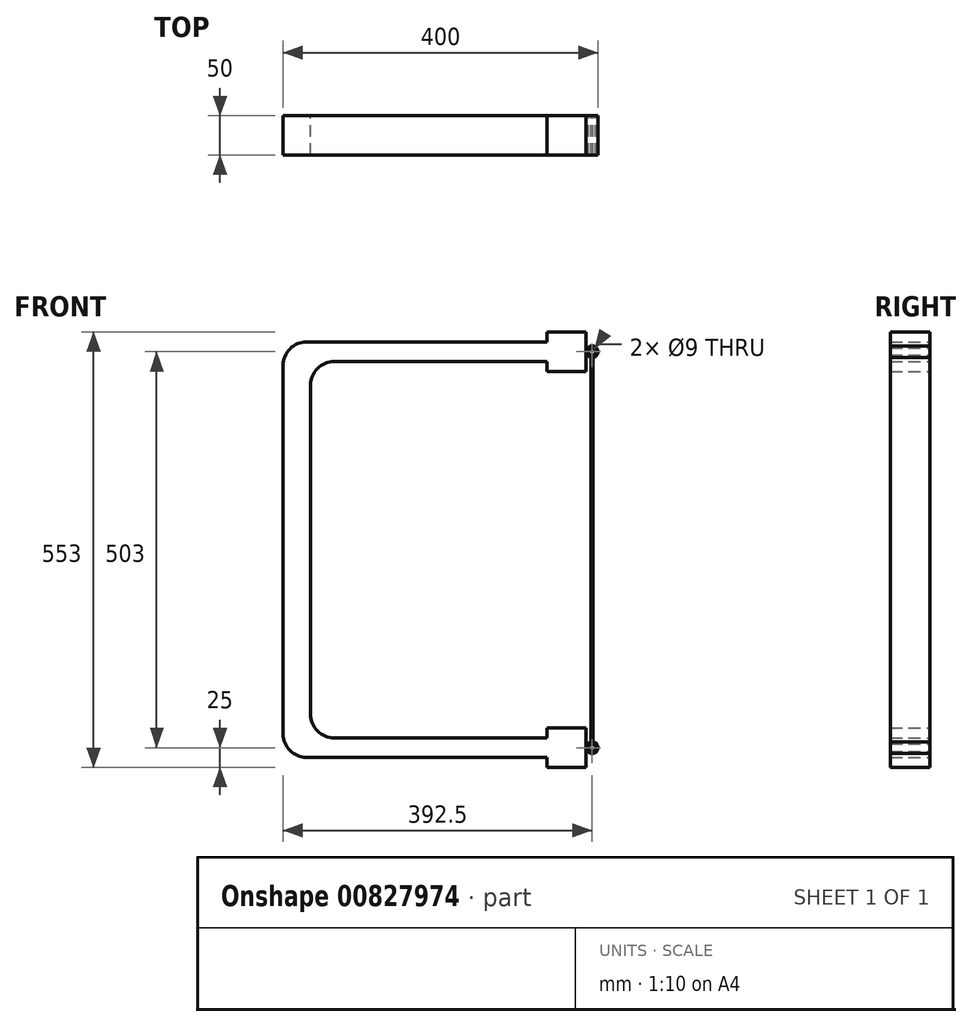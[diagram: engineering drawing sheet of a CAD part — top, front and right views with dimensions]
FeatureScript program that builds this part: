
annotation { "Feature Type Name" : "Feature", "Feature Type Description" : "" }
export const myFeature = defineFeature(function(context is Context, id is Id, definition is map)
    precondition{}
    {
        {
            var Q0;
            Q0=qCreatedBy(makeId("Front.planeOp"),FACE);
            var sketch = newSketch(context, id + "F0", { "sketchPlane" : qUnion([Q0])});
            skLineSegment(sketch, "E0.bottom", {"start": v(135, 264) * mm, "end": v(-170, 264) * mm});
            skLineSegment(sketch, "E0.left", {"start": v(200, 264) * mm, "end": v(200, 239) * mm, "construction": true});
            skLineSegment(sketch, "E0.right", {"start": v(-200, 234) * mm, "end": v(-200, -234) * mm});
            skPoint(sketch, "E0.middle", {"position": v(0, 0) * mm});
            skLineSegment(sketch, "E1.bottom", {"start": v(135, 239) * mm, "end": v(-135, 239) * mm});
            skLineSegment(sketch, "E1.top", {"start": v(135, -239) * mm, "end": v(-135, -239) * mm});
            skLineSegment(sketch, "E1.right", {"start": v(-165, 209) * mm, "end": v(-165, -209) * mm});
            skLineSegment(sketch, "E2.trimOffspring", {"start": v(200, -239) * mm, "end": v(200, -264) * mm, "construction": true});
            skPoint(sketch, "E3.visualSharp", {"position": v(-200, 264) * mm});
            skArc(sketch, "E3.filletArc", {"start": v(-170, 264) * mm, "mid": v(-191.21, 255.21) * mm, "end": v(-200, 234) * mm});
            skPoint(sketch, "E4.visualSharp", {"position": v(-165, 239) * mm});
            skArc(sketch, "E4.filletArc", {"start": v(-135, 239) * mm, "mid": v(-156.21, 230.21) * mm, "end": v(-165, 209) * mm});
            skPoint(sketch, "E5.visualSharp", {"position": v(-200, -264) * mm});
            skArc(sketch, "E5.filletArc", {"start": v(-200, -234) * mm, "mid": v(-191.21, -255.21) * mm, "end": v(-170, -264) * mm});
            skPoint(sketch, "E6.visualSharp", {"position": v(-165, -239) * mm});
            skArc(sketch, "E6.filletArc", {"start": v(-165, -209) * mm, "mid": v(-156.21, -230.21) * mm, "end": v(-135, -239) * mm});
            skLineSegment(sketch, "E7.top", {"start": v(185, 276.5) * mm, "end": v(135, 276.5) * mm});
            skLineSegment(sketch, "E7.right", {"start": v(135, 264) * mm, "end": v(135, 276.5) * mm});
            skLineSegment(sketch, "E8.top", {"start": v(185, 226.5) * mm, "end": v(135, 226.5) * mm});
            skLineSegment(sketch, "E8.right", {"start": v(135, 239) * mm, "end": v(135, 226.5) * mm});
            skLineSegment(sketch, "E9.top", {"start": v(185, -226.5) * mm, "end": v(135, -226.5) * mm});
            skLineSegment(sketch, "E9.right", {"start": v(135, -239) * mm, "end": v(135, -226.5) * mm});
            skLineSegment(sketch, "E10.top", {"start": v(185, -276.5) * mm, "end": v(140, -276.5) * mm});
            skLineSegment(sketch, "E11.bottom", {"start": v(135, 276.5) * mm, "end": v(185, 276.5) * mm});
            skLineSegment(sketch, "E11.left", {"start": v(135, 276.5) * mm, "end": v(135, 264) * mm});
            skLineSegment(sketch, "E11.right", {"start": v(185, 276.5) * mm, "end": v(185, 251.5) * mm});
            skLineSegment(sketch, "E12.left", {"start": v(185, 251.5) * mm, "end": v(185, 226.5) * mm});
            skLineSegment(sketch, "E13", {"start": v(200, 251.5) * mm, "end": v(185, 251.5) * mm, "construction": true});
            skCircle(sketch, "E14", {"center": v(192.5, 251.5) * mm, "radius": 7.5 * mm});
            skPoint(sketch, "E15.orphan", {"position": v(165, 239) * mm});
            skCircle(sketch, "E16", {"center": v(192.5, 251.5) * mm, "radius": 4.5 * mm});
            skLineSegment(sketch, "E17.top", {"start": v(135, -276.5) * mm, "end": v(185, -276.5) * mm});
            skLineSegment(sketch, "E17.left", {"start": v(135, -226.5) * mm, "end": v(135, -239) * mm});
            skLineSegment(sketch, "E17.right", {"start": v(185, -226.5) * mm, "end": v(185, -276.5) * mm});
            skLineSegment(sketch, "E18.trimOffspring", {"start": v(135, -264) * mm, "end": v(-170, -264) * mm});
            skLineSegment(sketch, "E19", {"start": v(200, -251.5) * mm, "end": v(185, -251.5) * mm, "construction": true});
            skCircle(sketch, "E20", {"center": v(192.5, -251.5) * mm, "radius": 7.5 * mm});
            skCircle(sketch, "E21", {"center": v(192.5, -251.5) * mm, "radius": 4.5 * mm});
            skLineSegment(sketch, "E22.trimOffspring", {"start": v(135, -264) * mm, "end": v(135, -276.5) * mm});
            skSolve(sketch);
        }
        {
            var Q0;
            Q0 = qSketchRegion(id + "F0", true);
            extrude(context, id + "F1", {"entities" : qUnion([Q0]), "depth" : 50 * mm, "offsetDistance" : 25 * mm});
        }
        {
            var Q0;
            Q0=qCreatedBy(makeId("Front.planeOp"),FACE);
            var sketch = newSketch(context, id + "F2", { "sketchPlane" : qUnion([Q0])});
            skLineSegment(sketch, "E23.bottom", {"start": v(191.33, 244) * mm, "end": v(193.33, 244) * mm});
            skLineSegment(sketch, "E23.top", {"start": v(191.33, -244) * mm, "end": v(193.33, -244) * mm});
            skLineSegment(sketch, "E23.left", {"start": v(193.33, 244) * mm, "end": v(193.33, -244) * mm});
            skLineSegment(sketch, "E23.right", {"start": v(191.33, 244) * mm, "end": v(191.33, -244) * mm});
            skPoint(sketch, "E24", {"position": v(192.33, 244) * mm});
            skSolve(sketch);
        }
        {
            var Q0;
            Q0 = qSketchRegion(id + "F2", true);
            extrude(context, id + "F3", {"entities" : qUnion([Q0]), "operationType" : NewBodyOperationType.ADD, "depth" : 50 * mm, "offsetDistance" : 25 * mm});
        }
    });
